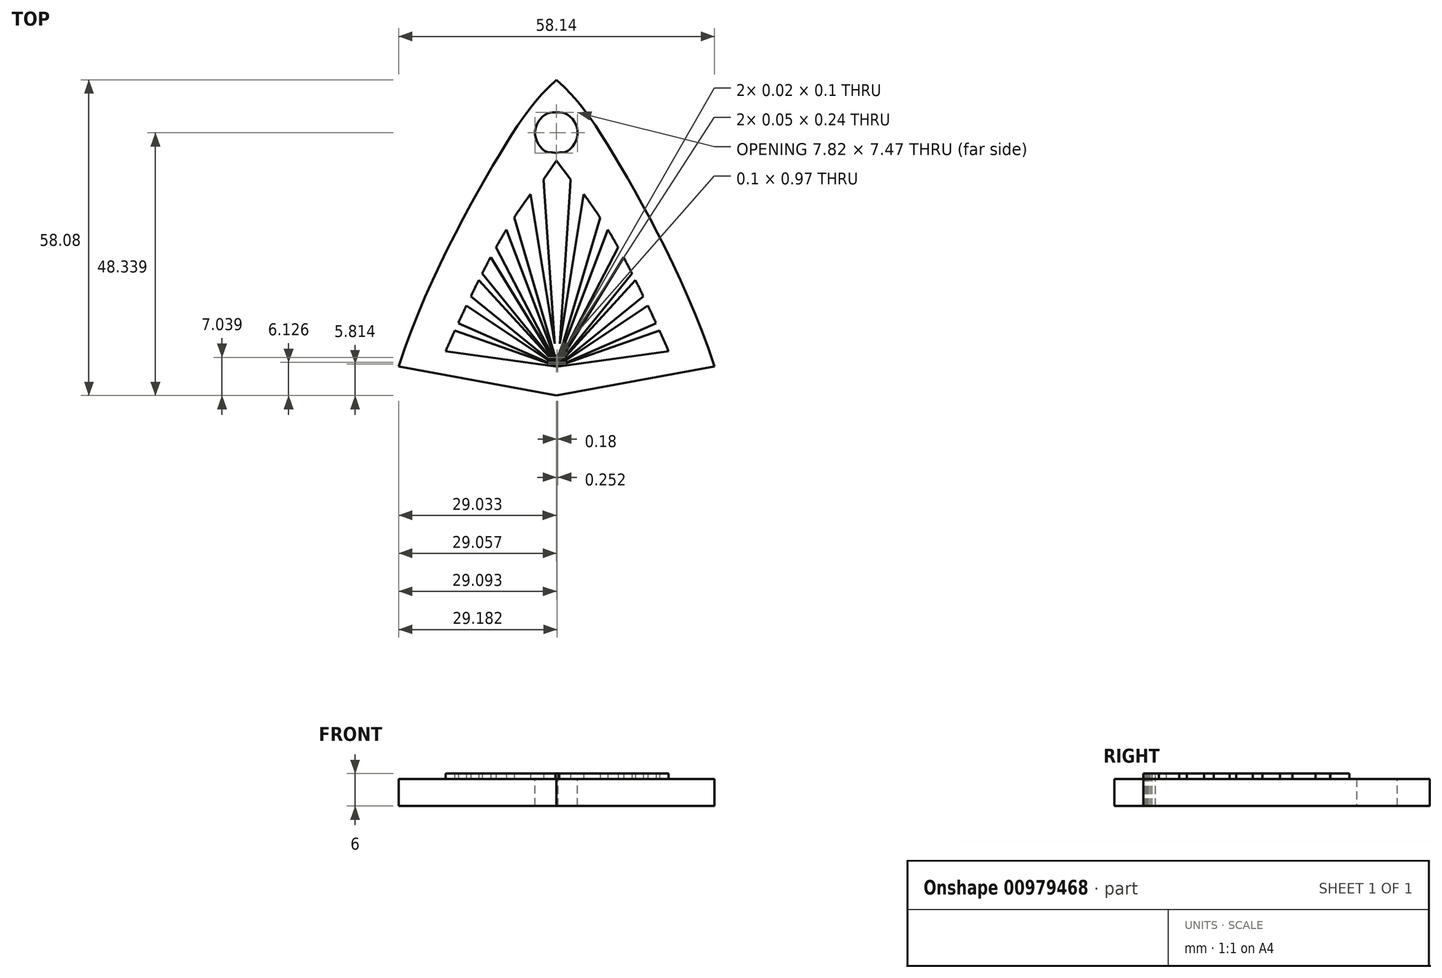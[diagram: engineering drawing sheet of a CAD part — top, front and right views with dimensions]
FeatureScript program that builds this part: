
annotation { "Feature Type Name" : "Feature", "Feature Type Description" : "" }
export const myFeature = defineFeature(function(context is Context, id is Id, definition is map)
    precondition{}
    {
        {
            var Q0;
            Q0=qCreatedBy(makeId("Top.planeOp"),FACE);
            var sketch = newSketch(context, id + "F0", { "sketchPlane" : qUnion([Q0])});
            skLineSegment(sketch, "E0", {"start": v(-29.07, -23.97) * mm, "end": v(-0.04, -29.31) * mm});
            skLineSegment(sketch, "E1", {"start": v(-0.04, -29.31) * mm, "end": v(29.07, -23.97) * mm});
            skLineSegment(sketch, "E2", {"start": v(0.32, -23.88) * mm, "end": v(0.32, -23.88) * mm});
            skLineSegment(sketch, "E3", {"start": v(0.32, -23.88) * mm, "end": v(18.3, -15.98) * mm});
            skLineSegment(sketch, "E4", {"start": v(16.82, -12.8) * mm, "end": v(0.33, -23.77) * mm});
            skLineSegment(sketch, "E5", {"start": v(0.33, -23.77) * mm, "end": v(0.33, -23.74) * mm});
            skLineSegment(sketch, "E6", {"start": v(0.33, -23.74) * mm, "end": v(15.98, -11.03) * mm});
            skLineSegment(sketch, "E7", {"start": v(14.52, -8.07) * mm, "end": v(0.34, -23.6) * mm});
            skLineSegment(sketch, "E8", {"start": v(0.34, -23.6) * mm, "end": v(0.34, -23.57) * mm});
            skLineSegment(sketch, "E9", {"start": v(0.34, -23.57) * mm, "end": v(13.9, -6.85) * mm});
            skLineSegment(sketch, "E10", {"start": v(12.33, -3.85) * mm, "end": v(0.35, -23.36) * mm});
            skLineSegment(sketch, "E11", {"start": v(0.35, -23.36) * mm, "end": v(0.36, -23.21) * mm});
            skLineSegment(sketch, "E12", {"start": v(0.36, -23.21) * mm, "end": v(11.34, -2.04) * mm});
            skLineSegment(sketch, "E13", {"start": v(9.45, 1.2) * mm, "end": v(0.4, -22.8) * mm});
            skLineSegment(sketch, "E14", {"start": v(0.4, -22.8) * mm, "end": v(0.42, -22.36) * mm});
            skLineSegment(sketch, "E15", {"start": v(0.42, -22.36) * mm, "end": v(8.02, 3.44) * mm});
            skLineSegment(sketch, "E16", {"start": v(5.01, 7.73) * mm, "end": v(0.6, -19.76) * mm});
            skLineSegment(sketch, "E17", {"start": v(0.6, -19.76) * mm, "end": v(2.53, 9.22) * mm});
            skLineSegment(sketch, "E18", {"start": v(2.53, 9.22) * mm, "end": v(2.6, 10.42) * mm});
            skLineSegment(sketch, "E19", {"start": v(2.6, 10.42) * mm, "end": v(2.59, 10.44) * mm});
            skLineSegment(sketch, "E20", {"start": v(2.59, 10.44) * mm, "end": v(2.61, 10.44) * mm});
            skLineSegment(sketch, "E21", {"start": v(2.61, 10.44) * mm, "end": v(-0.01, 13.92) * mm});
            skLineSegment(sketch, "E22", {"start": v(-0.01, 13.92) * mm, "end": v(-2.38, 10.44) * mm});
            skLineSegment(sketch, "E23", {"start": v(-2.38, 10.44) * mm, "end": v(-2.36, 10.44) * mm});
            skLineSegment(sketch, "E24", {"start": v(-2.36, 10.44) * mm, "end": v(-2.38, 10.42) * mm});
            skLineSegment(sketch, "E25", {"start": v(-2.38, 10.42) * mm, "end": v(-2.3, 9.22) * mm});
            skLineSegment(sketch, "E26", {"start": v(-2.3, 9.22) * mm, "end": v(-0.37, -19.76) * mm});
            skLineSegment(sketch, "E27", {"start": v(-0.37, -19.76) * mm, "end": v(-4.79, 7.73) * mm});
            skLineSegment(sketch, "E28", {"start": v(-7.8, 3.44) * mm, "end": v(-0.2, -22.36) * mm});
            skLineSegment(sketch, "E29", {"start": v(-0.2, -22.36) * mm, "end": v(-0.16, -22.8) * mm});
            skLineSegment(sketch, "E30", {"start": v(-0.16, -22.8) * mm, "end": v(-9.23, 1.2) * mm});
            skLineSegment(sketch, "E31", {"start": v(-11.12, -2.04) * mm, "end": v(-0.14, -23.21) * mm});
            skLineSegment(sketch, "E32", {"start": v(-0.14, -23.21) * mm, "end": v(-0.13, -23.36) * mm});
            skLineSegment(sketch, "E33", {"start": v(-0.13, -23.36) * mm, "end": v(-12.1, -3.85) * mm});
            skLineSegment(sketch, "E34", {"start": v(-13.68, -6.85) * mm, "end": v(-0.11, -23.57) * mm});
            skLineSegment(sketch, "E35", {"start": v(-0.11, -23.57) * mm, "end": v(-0.11, -23.6) * mm});
            skLineSegment(sketch, "E36", {"start": v(-0.11, -23.6) * mm, "end": v(-14.3, -8.07) * mm});
            skLineSegment(sketch, "E37", {"start": v(-15.75, -11.03) * mm, "end": v(-0.1, -23.74) * mm});
            skLineSegment(sketch, "E38", {"start": v(-0.1, -23.74) * mm, "end": v(-0.1, -23.77) * mm});
            skLineSegment(sketch, "E39", {"start": v(-0.1, -23.77) * mm, "end": v(-16.6, -12.8) * mm});
            skLineSegment(sketch, "E40", {"start": v(-18.08, -15.98) * mm, "end": v(-0.1, -23.88) * mm});
            skLineSegment(sketch, "E41", {"start": v(-0.1, -23.88) * mm, "end": v(-0.1, -23.88) * mm});
            skLineSegment(sketch, "E42", {"start": v(-0.1, -23.88) * mm, "end": v(-18.72, -17.38) * mm});
            skLineSegment(sketch, "E43", {"start": v(-20.4, -21.13) * mm, "end": v(-0.22, -23.97) * mm});
            skLineSegment(sketch, "E44", {"start": v(-0.22, -23.97) * mm, "end": v(-0.09, -23.97) * mm});
            skLineSegment(sketch, "E45", {"start": v(-0.09, -23.97) * mm, "end": v(-0.05, -23.97) * mm});
            skLineSegment(sketch, "E46", {"start": v(-0.05, -23.97) * mm, "end": v(-0.05, -23.97) * mm});
            skLineSegment(sketch, "E47", {"start": v(-0.05, -23.97) * mm, "end": v(-0.03, -23.97) * mm});
            skLineSegment(sketch, "E48", {"start": v(-0.03, -23.97) * mm, "end": v(-0.02, -23.97) * mm});
            skLineSegment(sketch, "E49", {"start": v(-0.02, -23.97) * mm, "end": v(0.24, -23.97) * mm});
            skLineSegment(sketch, "E50", {"start": v(0.24, -23.97) * mm, "end": v(0.25, -23.97) * mm});
            skLineSegment(sketch, "E51", {"start": v(0.25, -23.97) * mm, "end": v(0.28, -23.97) * mm});
            skLineSegment(sketch, "E52", {"start": v(0.28, -23.97) * mm, "end": v(0.28, -23.97) * mm});
            skLineSegment(sketch, "E53", {"start": v(0.28, -23.97) * mm, "end": v(0.31, -23.97) * mm});
            skLineSegment(sketch, "E54", {"start": v(0.31, -23.97) * mm, "end": v(0.45, -23.97) * mm});
            skLineSegment(sketch, "E55", {"start": v(0.45, -23.97) * mm, "end": v(20.62, -21.13) * mm});
            skLineSegment(sketch, "E56", {"start": v(18.95, -17.38) * mm, "end": v(0.32, -23.88) * mm});
            skLineSegment(sketch, "E57", {"start": v(0.24, -23.55) * mm, "end": v(0.23, -23.47) * mm});
            skLineSegment(sketch, "E58", {"start": v(0.23, -23.47) * mm, "end": v(0.24, -23.45) * mm});
            skLineSegment(sketch, "E59", {"start": v(0.24, -23.45) * mm, "end": v(0.25, -23.53) * mm});
            skLineSegment(sketch, "E60", {"start": v(0.25, -23.53) * mm, "end": v(0.24, -23.55) * mm});
            skLineSegment(sketch, "E61", {"start": v(0.22, -23.82) * mm, "end": v(0.23, -23.81) * mm});
            skLineSegment(sketch, "E62", {"start": v(0.23, -23.81) * mm, "end": v(0.24, -23.83) * mm});
            skLineSegment(sketch, "E63", {"start": v(0.24, -23.83) * mm, "end": v(0.23, -23.84) * mm});
            skLineSegment(sketch, "E64", {"start": v(0.23, -23.84) * mm, "end": v(0.22, -23.82) * mm});
            skLineSegment(sketch, "E65", {"start": v(0.2, -23.3) * mm, "end": v(0.18, -23.17) * mm});
            skLineSegment(sketch, "E66", {"start": v(0.18, -23.17) * mm, "end": v(0.21, -23.06) * mm});
            skLineSegment(sketch, "E67", {"start": v(0.21, -23.06) * mm, "end": v(0.23, -23.24) * mm});
            skLineSegment(sketch, "E68", {"start": v(0.23, -23.24) * mm, "end": v(0.2, -23.3) * mm});
            skLineSegment(sketch, "E69", {"start": v(0.21, -23.74) * mm, "end": v(0.2, -23.75) * mm});
            skLineSegment(sketch, "E70", {"start": v(0.2, -23.75) * mm, "end": v(0.2, -23.75) * mm});
            skLineSegment(sketch, "E71", {"start": v(0.2, -23.75) * mm, "end": v(0.2, -23.72) * mm});
            skLineSegment(sketch, "E72", {"start": v(0.2, -23.72) * mm, "end": v(0.21, -23.74) * mm});
            skLineSegment(sketch, "E73", {"start": v(0.18, -23.86) * mm, "end": v(0.2, -23.85) * mm});
            skLineSegment(sketch, "E74", {"start": v(0.2, -23.85) * mm, "end": v(0.2, -23.86) * mm});
            skLineSegment(sketch, "E75", {"start": v(0.2, -23.86) * mm, "end": v(0.18, -23.87) * mm});
            skLineSegment(sketch, "E76", {"start": v(0.18, -23.87) * mm, "end": v(0.18, -23.86) * mm});
            skLineSegment(sketch, "E77", {"start": v(0.16, -23.67) * mm, "end": v(0.15, -23.63) * mm});
            skLineSegment(sketch, "E78", {"start": v(0.15, -23.63) * mm, "end": v(0.17, -23.59) * mm});
            skLineSegment(sketch, "E79", {"start": v(0.17, -23.59) * mm, "end": v(0.18, -23.64) * mm});
            skLineSegment(sketch, "E80", {"start": v(0.18, -23.64) * mm, "end": v(0.16, -23.67) * mm});
            skLineSegment(sketch, "E81", {"start": v(0.11, -22.75) * mm, "end": v(0.06, -22.44) * mm});
            skLineSegment(sketch, "E82", {"start": v(0.06, -22.44) * mm, "end": v(0.11, -21.79) * mm});
            skLineSegment(sketch, "E83", {"start": v(0.11, -21.79) * mm, "end": v(0.16, -22.44) * mm});
            skLineSegment(sketch, "E84", {"start": v(0.16, -22.44) * mm, "end": v(0.11, -22.75) * mm});
            skLineSegment(sketch, "E85", {"start": v(0.14, -23.8) * mm, "end": v(0.16, -23.79) * mm});
            skLineSegment(sketch, "E86", {"start": v(0.16, -23.79) * mm, "end": v(0.16, -23.79) * mm});
            skLineSegment(sketch, "E87", {"start": v(0.16, -23.79) * mm, "end": v(0.15, -23.8) * mm});
            skLineSegment(sketch, "E88", {"start": v(0.15, -23.8) * mm, "end": v(0.14, -23.8) * mm});
            skLineSegment(sketch, "E89", {"start": v(0.11, -23.91) * mm, "end": v(0.11, -23.91) * mm});
            skLineSegment(sketch, "E90", {"start": v(0.11, -23.91) * mm, "end": v(0.12, -23.91) * mm});
            skLineSegment(sketch, "E91", {"start": v(0.12, -23.91) * mm, "end": v(0.11, -23.91) * mm});
            skLineSegment(sketch, "E92", {"start": v(0.1, -23.73) * mm, "end": v(0.11, -23.7) * mm});
            skLineSegment(sketch, "E93", {"start": v(0.11, -23.7) * mm, "end": v(0.13, -23.73) * mm});
            skLineSegment(sketch, "E94", {"start": v(0.13, -23.73) * mm, "end": v(0.11, -23.75) * mm});
            skLineSegment(sketch, "E95", {"start": v(0.11, -23.75) * mm, "end": v(0.1, -23.73) * mm});
            skLineSegment(sketch, "E96", {"start": v(0.1, -23.48) * mm, "end": v(0.11, -23.4) * mm});
            skLineSegment(sketch, "E97", {"start": v(0.11, -23.4) * mm, "end": v(0.14, -23.48) * mm});
            skLineSegment(sketch, "E98", {"start": v(0.14, -23.48) * mm, "end": v(0.11, -23.54) * mm});
            skLineSegment(sketch, "E99", {"start": v(0.11, -23.54) * mm, "end": v(0.1, -23.48) * mm});
            skLineSegment(sketch, "E100", {"start": v(0.06, -23.79) * mm, "end": v(0.06, -23.79) * mm});
            skLineSegment(sketch, "E101", {"start": v(0.06, -23.79) * mm, "end": v(0.08, -23.8) * mm});
            skLineSegment(sketch, "E102", {"start": v(0.08, -23.8) * mm, "end": v(0.08, -23.8) * mm});
            skLineSegment(sketch, "E103", {"start": v(0.08, -23.8) * mm, "end": v(0.06, -23.79) * mm});
            skLineSegment(sketch, "E104", {"start": v(0.06, -23.67) * mm, "end": v(0.04, -23.64) * mm});
            skLineSegment(sketch, "E105", {"start": v(0.04, -23.64) * mm, "end": v(0.06, -23.59) * mm});
            skLineSegment(sketch, "E106", {"start": v(0.06, -23.59) * mm, "end": v(0.08, -23.63) * mm});
            skLineSegment(sketch, "E107", {"start": v(0.08, -23.63) * mm, "end": v(0.06, -23.67) * mm});
            skLineSegment(sketch, "E108", {"start": v(0.02, -23.3) * mm, "end": v(0, -23.24) * mm});
            skLineSegment(sketch, "E109", {"start": v(0, -23.24) * mm, "end": v(0.01, -23.06) * mm});
            skLineSegment(sketch, "E110", {"start": v(0.01, -23.06) * mm, "end": v(0.05, -23.17) * mm});
            skLineSegment(sketch, "E111", {"start": v(0.05, -23.17) * mm, "end": v(0.02, -23.3) * mm});
            skLineSegment(sketch, "E112", {"start": v(0.03, -23.86) * mm, "end": v(0.03, -23.85) * mm});
            skLineSegment(sketch, "E113", {"start": v(0.03, -23.85) * mm, "end": v(0.05, -23.86) * mm});
            skLineSegment(sketch, "E114", {"start": v(0.05, -23.86) * mm, "end": v(0.04, -23.87) * mm});
            skLineSegment(sketch, "E115", {"start": v(0.04, -23.87) * mm, "end": v(0.03, -23.86) * mm});
            skLineSegment(sketch, "E116", {"start": v(0.01, -23.74) * mm, "end": v(0.02, -23.72) * mm});
            skLineSegment(sketch, "E117", {"start": v(0.02, -23.72) * mm, "end": v(0.03, -23.75) * mm});
            skLineSegment(sketch, "E118", {"start": v(0.03, -23.75) * mm, "end": v(0.03, -23.75) * mm});
            skLineSegment(sketch, "E119", {"start": v(0.03, -23.75) * mm, "end": v(0.01, -23.74) * mm});
            skLineSegment(sketch, "E120", {"start": v(-0.01, -23.83) * mm, "end": v(0, -23.81) * mm});
            skLineSegment(sketch, "E121", {"start": v(0, -23.81) * mm, "end": v(0, -23.82) * mm});
            skLineSegment(sketch, "E122", {"start": v(0, -23.82) * mm, "end": v(0, -23.84) * mm});
            skLineSegment(sketch, "E123", {"start": v(0, -23.84) * mm, "end": v(-0.01, -23.83) * mm});
            skLineSegment(sketch, "E124", {"start": v(-0.02, -23.53) * mm, "end": v(-0.02, -23.45) * mm});
            skLineSegment(sketch, "E125", {"start": v(-0.02, -23.45) * mm, "end": v(0, -23.47) * mm});
            skLineSegment(sketch, "E126", {"start": v(0, -23.47) * mm, "end": v(-0.02, -23.55) * mm});
            skLineSegment(sketch, "E127", {"start": v(-0.02, -23.55) * mm, "end": v(-0.02, -23.53) * mm});
            skFitSpline(sketch, "E128", {"points": [v(-0.04, 15.3) * mm, v(0.62, 15.4) * mm, v(1.92, 15.6) * mm, v(3.35, 17.09) * mm, v(3.87, 19.03) * mm, v(3.35, 20.98) * mm, v(1.92, 22.41) * mm, v(0.62, 22.76) * mm, v(-0.04, 22.76) * mm, v(-0.04, 22.76) * mm]});
            skFitSpline(sketch, "E129", {"points": [v(-0.04, 22.76) * mm, v(-0.7, 22.76) * mm, v(-2, 22.41) * mm, v(-3.42, 20.98) * mm, v(-3.95, 19.03) * mm, v(-3.42, 17.09) * mm, v(-2, 15.6) * mm, v(-0.7, 15.4) * mm, v(-0.04, 15.3) * mm]});
            skFitSpline(sketch, "E130", {"points": [v(18.3, -15.98) * mm, v(18.15, -15.64) * mm, v(17.83, -14.94) * mm, v(17.33, -13.88) * mm, v(17, -13.16) * mm, v(16.82, -12.8) * mm]});
            skFitSpline(sketch, "E131", {"points": [v(15.98, -11.03) * mm, v(15.82, -10.7) * mm, v(15.5, -10.05) * mm, v(15.01, -9.06) * mm, v(14.68, -8.4) * mm, v(14.52, -8.07) * mm]});
            skFitSpline(sketch, "E132", {"points": [v(13.9, -6.85) * mm, v(13.73, -6.52) * mm, v(13.39, -5.85) * mm, v(12.86, -4.85) * mm, v(12.5, -4.18) * mm, v(12.33, -3.85) * mm]});
            skFitSpline(sketch, "E133", {"points": [v(11.34, -2.04) * mm, v(11.13, -1.67) * mm, v(10.72, -0.93) * mm, v(10.1, 0.15) * mm, v(9.66, 0.85) * mm, v(9.45, 1.2) * mm]});
            skFitSpline(sketch, "E134", {"points": [v(8.02, 3.44) * mm, v(7.7, 3.91) * mm, v(7.06, 4.87) * mm, v(6.05, 6.3) * mm, v(5.36, 7.25) * mm, v(5.01, 7.73) * mm]});
            skFitSpline(sketch, "E135", {"points": [v(-4.79, 7.73) * mm, v(-5.14, 7.25) * mm, v(-5.83, 6.3) * mm, v(-6.83, 4.87) * mm, v(-7.48, 3.91) * mm, v(-7.8, 3.44) * mm]});
            skFitSpline(sketch, "E136", {"points": [v(-9.23, 1.2) * mm, v(-9.44, 0.85) * mm, v(-9.86, 0.15) * mm, v(-10.5, -0.93) * mm, v(-10.9, -1.67) * mm, v(-11.12, -2.04) * mm]});
            skFitSpline(sketch, "E137", {"points": [v(-12.1, -3.85) * mm, v(-12.28, -4.18) * mm, v(-12.64, -4.85) * mm, v(-13.16, -5.85) * mm, v(-13.5, -6.52) * mm, v(-13.68, -6.85) * mm]});
            skFitSpline(sketch, "E138", {"points": [v(-14.3, -8.07) * mm, v(-14.46, -8.4) * mm, v(-14.79, -9.06) * mm, v(-15.27, -10.05) * mm, v(-15.6, -10.7) * mm, v(-15.75, -11.03) * mm]});
            skFitSpline(sketch, "E139", {"points": [v(-16.6, -12.8) * mm, v(-16.77, -13.16) * mm, v(-17.1, -13.88) * mm, v(-17.6, -14.94) * mm, v(-17.93, -15.64) * mm, v(-18.08, -15.98) * mm]});
            skFitSpline(sketch, "E140", {"points": [v(-18.72, -17.38) * mm, v(-18.93, -17.84) * mm, v(-19.33, -18.72) * mm, v(-19.88, -19.97) * mm, v(-20.23, -20.76) * mm, v(-20.4, -21.13) * mm]});
            skFitSpline(sketch, "E141", {"points": [v(20.62, -21.13) * mm, v(20.46, -20.76) * mm, v(20.1, -19.97) * mm, v(19.55, -18.72) * mm, v(19.15, -17.84) * mm, v(18.95, -17.38) * mm]});
            skFitSpline(sketch, "E142", {"points": [v(0, 28.77) * mm, v(10.33, 15.3) * mm, v(29.07, -23.97) * mm], "startDerivative": vector(34.3, -31) * mm, "endDerivative": vector(24.43, -75.18) * mm});
            skLineSegment(sketch, "E143", {"start": v(0, 28.77) * mm, "end": v(0, 35.24) * mm});
            skPoint(sketch, "E144.1.internal.orphan", {"position": v(-10.83, 15.3) * mm});
            skFitSpline(sketch, "E145.MirrorCS", {"points": [v(0, 28.77) * mm, v(-10.33, 15.3) * mm, v(-29.07, -23.97) * mm], "startDerivative": vector(-34.3, -31) * mm, "endDerivative": vector(-24.43, -75.18) * mm});
            skSolve(sketch);
        }
        {
            var Q0;
            Q0=makeQuery(id+"F0.imprint","IMPRINT",FACE,{"disambiguationData":[TD([[makeQuery(id+"F0.imprint","IMPRINT",EDGE,{"derivedFrom":sQuery(id+"F0.wireOp",EDGE,"E0")}),1.0]])]});
            extrude(context, id + "F1", {"entities" : qUnion([Q0]), "depth" : 5 * mm, "offsetDistance" : 25 * mm});
        }
        {
            var Q0;
            Q0=makeQuery(id+"F0.imprint","IMPRINT",FACE,{"disambiguationData":[TD([[makeQuery(id+"F0.imprint","IMPRINT",EDGE,{"derivedFrom":sQuery(id+"F0.wireOp",EDGE,"E2")}),1.0]])]});
            extrude(context, id + "F2", {"entities" : qUnion([Q0]), "operationType" : NewBodyOperationType.ADD, "depth" : 6 * mm, "offsetDistance" : 25 * mm});
        }
    });
